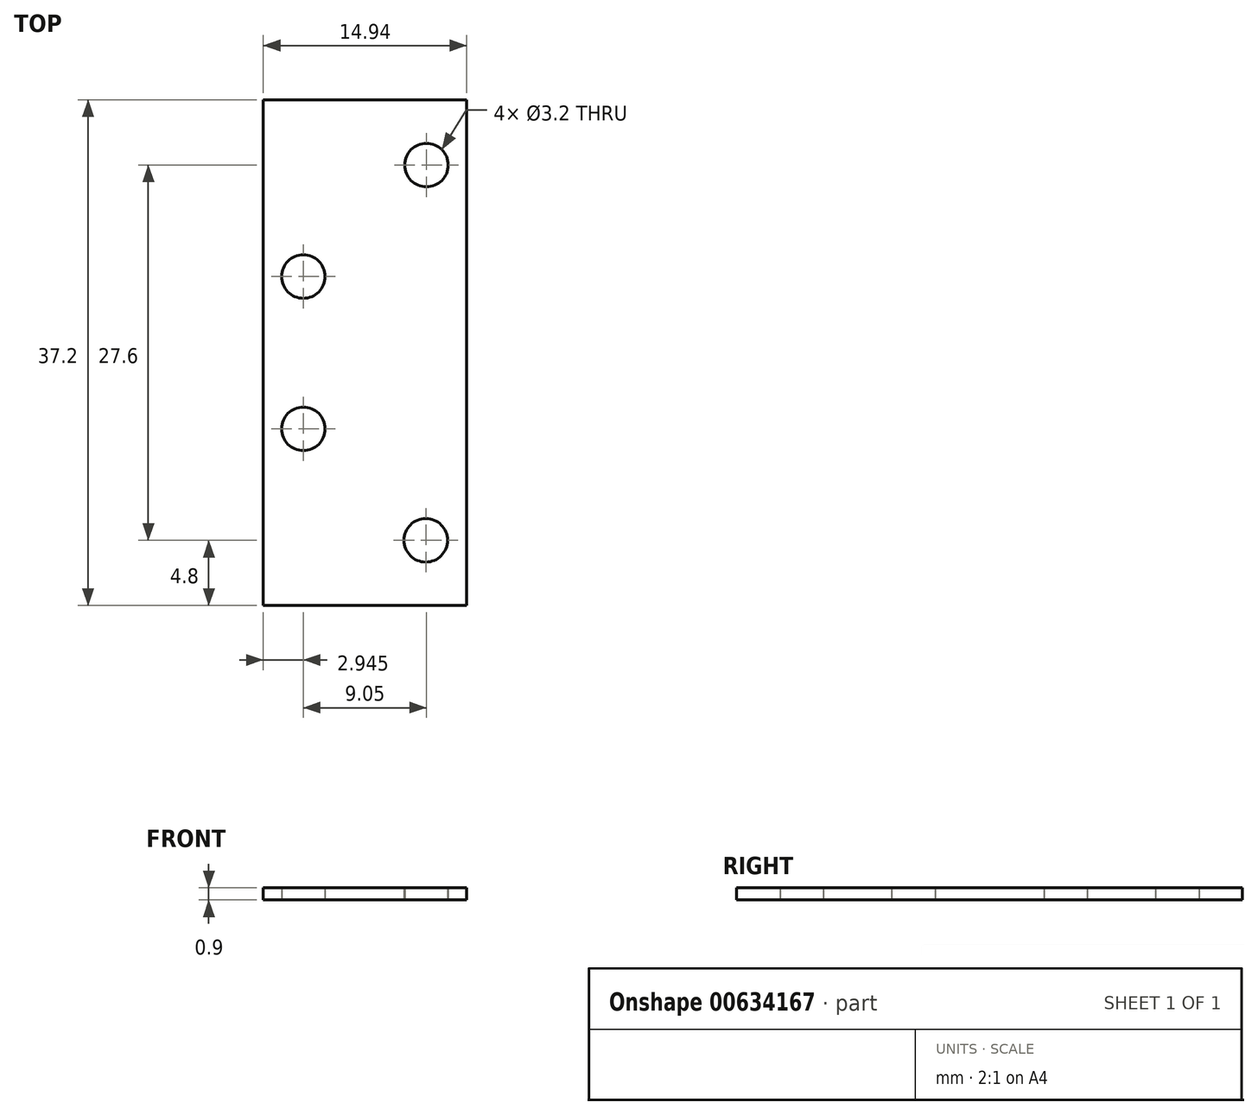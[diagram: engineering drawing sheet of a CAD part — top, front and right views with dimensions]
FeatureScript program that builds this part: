
annotation { "Feature Type Name" : "Feature", "Feature Type Description" : "" }
export const myFeature = defineFeature(function(context is Context, id is Id, definition is map)
    precondition{}
    {
        {
            var Q0;
            Q0=qCreatedBy(makeId("Top.planeOp"),FACE);
            var sketch = newSketch(context, id + "F0", { "sketchPlane" : qUnion([Q0])});
            skLineSegment(sketch, "E0", {"start": v(-7.48, -18.6) * mm, "end": v(7.48, -18.6) * mm});
            skLineSegment(sketch, "E1", {"start": v(7.48, -18.6) * mm, "end": v(7.48, 18.6) * mm});
            skLineSegment(sketch, "E2", {"start": v(7.48, 18.6) * mm, "end": v(-7.48, 18.6) * mm});
            skLineSegment(sketch, "E3", {"start": v(-7.48, 18.6) * mm, "end": v(-7.48, -18.6) * mm});
            skCircle(sketch, "E4", {"center": v(4.52, 13.8) * mm, "radius": 1.6 * mm});
            skCircle(sketch, "E5", {"center": v(-4.52, 5.6) * mm, "radius": 1.6 * mm});
            skCircle(sketch, "E6", {"center": v(-4.52, -5.6) * mm, "radius": 1.6 * mm});
            skCircle(sketch, "E7", {"center": v(4.48, -13.8) * mm, "radius": 1.6 * mm});
            skSolve(sketch);
        }
        {
            var Q0;
            Q0=makeQuery(id+"F0.imprint","IMPRINT",FACE,{"disambiguationData":[TD([[makeQuery(id+"F0.imprint","IMPRINT",EDGE,{"derivedFrom":sQuery(id+"F0.wireOp",EDGE,"E0")}),1.0]])]});
            extrude(context, id + "F1", {"entities" : qUnion([Q0]), "depth" : 0.9 * mm, "offsetDistance" : 25 * mm});
        }
    });
